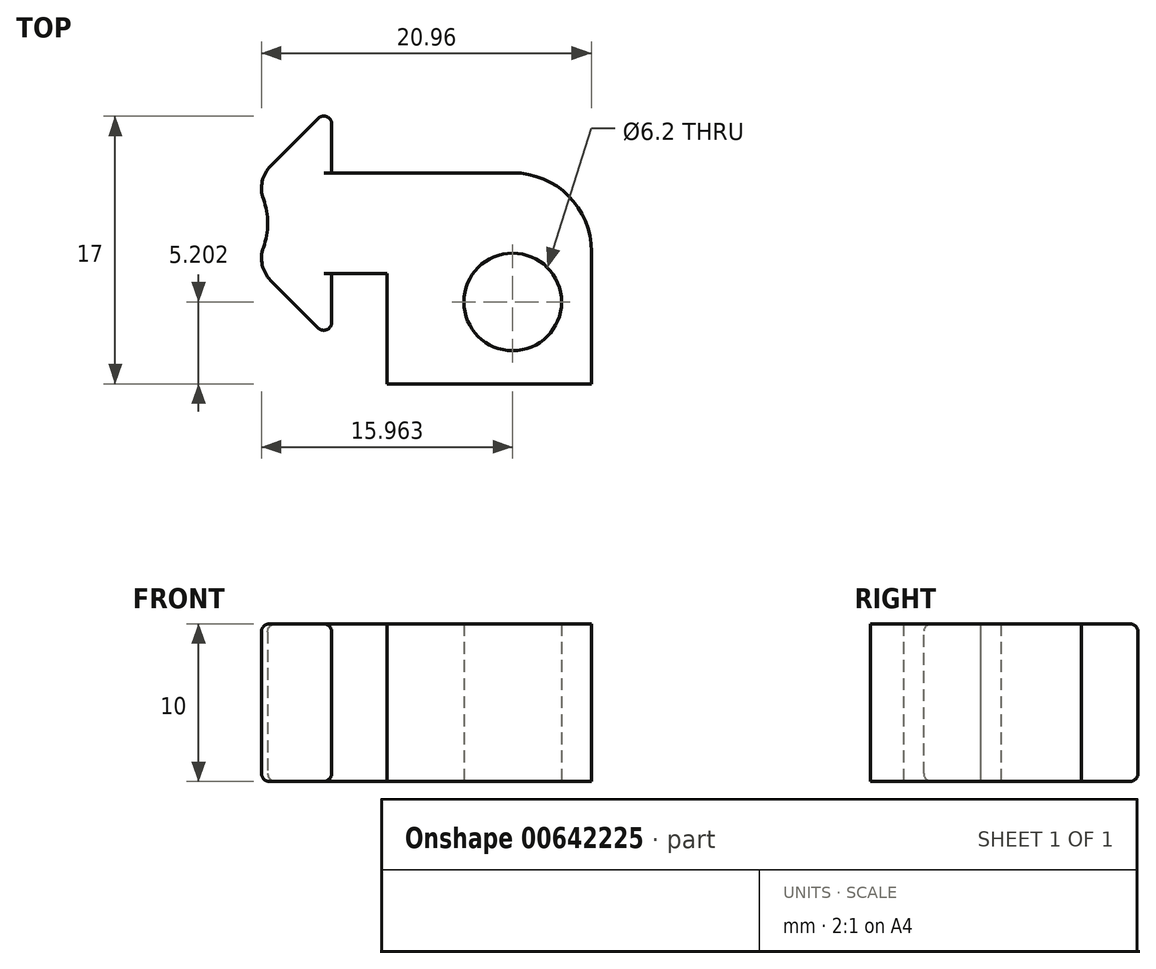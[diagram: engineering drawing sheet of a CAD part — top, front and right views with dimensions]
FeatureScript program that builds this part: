
annotation { "Feature Type Name" : "Feature", "Feature Type Description" : "" }
export const myFeature = defineFeature(function(context is Context, id is Id, definition is map)
    precondition{}
    {
        {
            var Q0;
            Q0=qCreatedBy(makeId("Top.planeOp"),FACE);
            var sketch = newSketch(context, id + "F0", { "sketchPlane" : qUnion([Q0])});
            skLineSegment(sketch, "E0", {"start": v(3.63, 2.54) * mm, "end": v(8.53, 7.44) * mm});
            skLineSegment(sketch, "E1", {"start": v(8.53, 7.44) * mm, "end": v(8.53, 3.13) * mm});
            skLineSegment(sketch, "E2", {"start": v(8.53, 3.13) * mm, "end": v(10.03, 3.13) * mm});
            skLineSegment(sketch, "E3", {"start": v(8.53, -7.58) * mm, "end": v(8.53, -3.27) * mm});
            skLineSegment(sketch, "E4", {"start": v(8.53, -3.27) * mm, "end": v(10.03, -3.27) * mm});
            skLineSegment(sketch, "E5", {"start": v(8.53, -7.58) * mm, "end": v(3.63, -2.68) * mm});
            skLineSegment(sketch, "E6", {"start": v(10.03, 3.13) * mm, "end": v(10.03, -3.27) * mm});
            skArc(sketch, "E7", {"start": v(3.63, -2.68) * mm, "mid": v(4.47, -0.07) * mm, "end": v(3.63, 2.54) * mm});
            skSolve(sketch);
        }
        {
            var Q0;
            Q0=makeQuery(id+"F0.imprint","IMPRINT",FACE,{"disambiguationData":[TD([[makeQuery(id+"F0.imprint","IMPRINT",EDGE,{"derivedFrom":sQuery(id+"F0.wireOp",EDGE,"E0")}),-1.0]])]});
            extrude(context, id + "F1", {"entities" : qUnion([Q0]), "depth" : 10 * mm, "offsetDistance" : 25 * mm});
        }
        {
            var Q0;
            Q0=makeQuery(id+"F1.opExtrude","SWEPT_EDGE",EDGE,{"disambiguationData":[OSD([sQuery(id+"F0.wireOp",EDGE,"E0"),sQuery(id+"F0.wireOp",EDGE,"E1")])]});
            var Q1;
            Q1=makeQuery(id+"F1.opExtrude","SWEPT_EDGE",EDGE,{"disambiguationData":[OSD([sQuery(id+"F0.wireOp",EDGE,"E3"),sQuery(id+"F0.wireOp",EDGE,"E5")])]});
            var Q2;
            Q2=makeQuery(id+"F1.opExtrude","CAP_EDGE",EDGE,{"disambiguationData":[OSD([sQuery(id+"F0.wireOp",EDGE,"E0")])],"isStart":true});
            var Q3;
            Q3=makeQuery(id+"F1.opExtrude","CAP_EDGE",EDGE,{"disambiguationData":[OSD([sQuery(id+"F0.wireOp",EDGE,"E1")])],"isStart":true});
            var Q4;
            Q4=makeQuery(id+"F1.opExtrude","CAP_EDGE",EDGE,{"disambiguationData":[OSD([sQuery(id+"F0.wireOp",EDGE,"E1")])],"isStart":false});
            var Q5;
            Q5=makeQuery(id+"F1.opExtrude","CAP_EDGE",EDGE,{"disambiguationData":[OSD([sQuery(id+"F0.wireOp",EDGE,"E0")])],"isStart":false});
            var Q6;
            Q6=makeQuery(id+"F1.opExtrude","CAP_EDGE",EDGE,{"disambiguationData":[OSD([sQuery(id+"F0.wireOp",EDGE,"E7")])],"isStart":false});
            var Q7;
            Q7=makeQuery(id+"F1.opExtrude","CAP_EDGE",EDGE,{"disambiguationData":[OSD([sQuery(id+"F0.wireOp",EDGE,"E5")])],"isStart":false});
            var Q8;
            Q8=makeQuery(id+"F1.opExtrude","CAP_EDGE",EDGE,{"disambiguationData":[OSD([sQuery(id+"F0.wireOp",EDGE,"E3")])],"isStart":false});
            var Q9;
            Q9=makeQuery(id+"F1.opExtrude","CAP_EDGE",EDGE,{"disambiguationData":[OSD([sQuery(id+"F0.wireOp",EDGE,"E7")])],"isStart":true});
            var Q10;
            Q10=makeQuery(id+"F1.opExtrude","CAP_EDGE",EDGE,{"disambiguationData":[OSD([sQuery(id+"F0.wireOp",EDGE,"E5")])],"isStart":true});
            var Q11;
            Q11=makeQuery(id+"F1.opExtrude","CAP_EDGE",EDGE,{"disambiguationData":[OSD([sQuery(id+"F0.wireOp",EDGE,"E3")])],"isStart":true});
            fillet(context, id + "F2", {"entities" : qUnion([Q0, Q1, Q2, Q3, Q4, Q5, Q6, Q7, Q8, Q9, Q10, Q11]), "radius" : 0.5 * mm, "tangentPropagation" : true, "allowEdgeOverflow" : false});
        }
        {
            var Q0;
            Q0=makeQuery(id+"F1.opExtrude","SWEPT_EDGE",EDGE,{"disambiguationData":[OSD([sQuery(id+"F0.wireOp",EDGE,"E0"),sQuery(id+"F0.wireOp",EDGE,"E7")])]});
            var Q1;
            Q1=makeQuery(id+"F1.opExtrude","SWEPT_EDGE",EDGE,{"disambiguationData":[OSD([sQuery(id+"F0.wireOp",EDGE,"E5"),sQuery(id+"F0.wireOp",EDGE,"E7")])]});
            fillet(context, id + "F3", {"entities" : qUnion([Q0, Q1]), "radius" : 2 * mm, "tangentPropagation" : true, "allowEdgeOverflow" : false});
        }
        {
            var Q0;
            Q0=makeQuery(id+"F1.opExtrude","SWEPT_FACE",FACE,{"disambiguationData":[OSD([sQuery(id+"F0.wireOp",EDGE,"E6")])]});
            extrude(context, id + "F4", {"entities" : qUnion([Q0]), "operationType" : NewBodyOperationType.ADD, "depth" : 15 * mm, "offsetDistance" : 25 * mm});
        }
        {
            var Q0;
            {var subQ0=sQuery(id+"F0.wireOp",EDGE,"E4");Q0=makeQuery(id+"F4.boolean.opBoolean","MERGE",FACE,{"derivedFrom":[makeQuery(id+"F1.opExtrude","SWEPT_FACE",FACE,{"disambiguationData":[OSD([subQ0])]}),makeQuery(id+"F4.opExtrude","SWEPT_FACE",FACE,{"disambiguationData":[OSD([subQ0,sQuery(id+"F0.wireOp",EDGE,"E6")])]})]});}
            var sketch = newSketch(context, id + "F5", { "sketchPlane" : qUnion([Q0])});
            skLineSegment(sketch, "E8.bottom", {"start": v(25.03, 10) * mm, "end": v(12.03, 10) * mm});
            skLineSegment(sketch, "E8.top", {"start": v(25.03, 0) * mm, "end": v(12.03, 0) * mm});
            skLineSegment(sketch, "E8.left", {"start": v(25.03, 10) * mm, "end": v(25.03, 0) * mm});
            skLineSegment(sketch, "E8.right", {"start": v(12.03, 10) * mm, "end": v(12.03, 0) * mm});
            skSolve(sketch);
        }
        {
            var Q0;
            Q0=makeQuery(id+"F5.imprint","IMPRINT",FACE,{"disambiguationData":[TD([[makeQuery(id+"F5.imprint","IMPRINT",EDGE,{"derivedFrom":sQuery(id+"F5.wireOp",EDGE,"E8.bottom")}),-1.0]])]});
            extrude(context, id + "F6", {"entities" : qUnion([Q0]), "operationType" : NewBodyOperationType.ADD, "depth" : 7 * mm, "offsetDistance" : 25 * mm});
        }
        {
            var Q0;
            Q0=makeQuery(id+"F4.opExtrude","CAP_EDGE",EDGE,{"disambiguationData":[OSD([sQuery(id+"F0.wireOp",EDGE,"E2"),sQuery(id+"F0.wireOp",EDGE,"E6")])],"isStart":false});
            fillet(context, id + "F7", {"entities" : qUnion([Q0]), "radius" : 5 * mm, "tangentPropagation" : true, "allowEdgeOverflow" : false});
        }
        {
            var Q0;
            {var subQ0=sQuery(id+"F0.wireOp",EDGE,"E6");Q0=makeQuery(id+"F6.boolean.opBoolean","MERGE",FACE,{"derivedFrom":[makeQuery(id+"F4.boolean.opBoolean","MERGE",FACE,{"derivedFrom":[makeQuery(id+"F1.opExtrude","CAP_FACE",FACE,{"disambiguationData":[OSD([sQuery(id+"F0.wireOp",EDGE,"E0"),sQuery(id+"F0.wireOp",EDGE,"E1"),sQuery(id+"F0.wireOp",EDGE,"E2"),sQuery(id+"F0.wireOp",EDGE,"E3"),sQuery(id+"F0.wireOp",EDGE,"E4"),sQuery(id+"F0.wireOp",EDGE,"E5"),subQ0,sQuery(id+"F0.wireOp",EDGE,"E7")])],"isStart":true}),makeQuery(id+"F4.opExtrude","SWEPT_FACE",FACE,{"disambiguationData":[OSD([subQ0]),TDD([makeQuery(id+"F1.opExtrude","CAP_EDGE",EDGE,{"disambiguationData":[OSD([subQ0])],"isStart":true})])]})]}),makeQuery(id+"F6.opExtrude","SWEPT_FACE",FACE,{"disambiguationData":[OSD([sQuery(id+"F5.wireOp",EDGE,"E8.top")])]})]});}
            var sketch = newSketch(context, id + "F8", { "sketchPlane" : qUnion([Q0])});
            skCircle(sketch, "E9", {"center": v(20.03, 5.07) * mm, "radius": 3.1 * mm});
            skSolve(sketch);
        }
        {
            var Q0;
            Q0=makeQuery(id+"F8.imprint","IMPRINT",FACE,{"disambiguationData":[TD([[makeQuery(id+"F8.imprint","IMPRINT",EDGE,{"derivedFrom":sQuery(id+"F8.wireOp",EDGE,"E9")}),1.0]])]});
            extrude(context, id + "F9", {"entities" : qUnion([Q0]), "operationType" : NewBodyOperationType.REMOVE, "oppositeDirection" : true, "depth" : 25 * mm, "offsetDistance" : 25 * mm});
        }
    });
